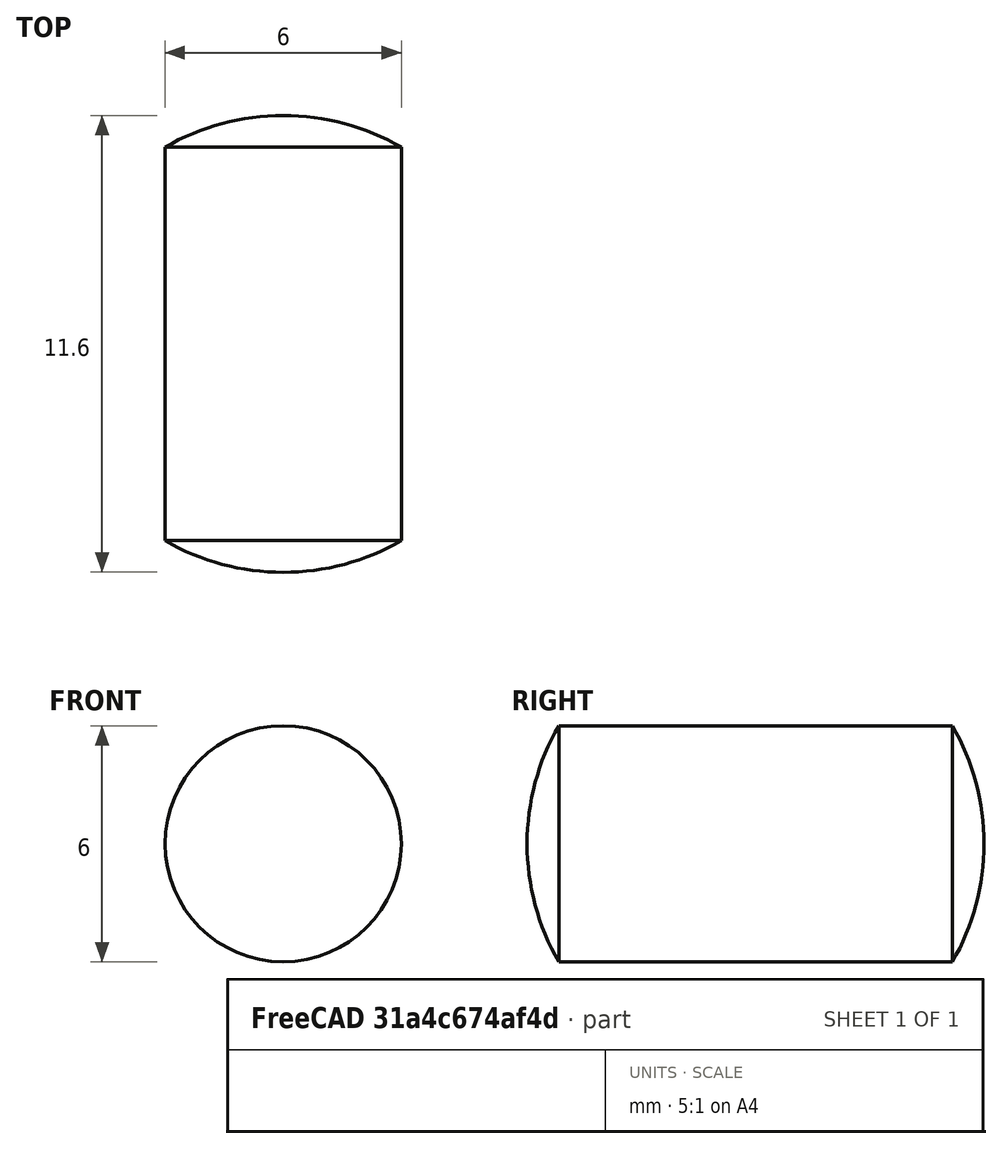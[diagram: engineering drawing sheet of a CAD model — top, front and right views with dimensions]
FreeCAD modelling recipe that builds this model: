
FCSTD DOCUMENT  (FreeCAD 0.15R4470 (Git))
Label: Zyl-Stift_DIN_7-6x10
License: CC-BY 3.0
LicenseURL: http://creativecommons.org/licenses/by/3.0/
objects: Sketcher::SketchObject×1, PartDesign::Revolution×1
note: 3 computed .brp shape members not serialized (recipe doc carries the construction recipe); baked Part::Feature solids carry a one-line shape summary decoded from their .brp

FEATURE [Sketcher::SketchObject] Sketch
  Placement = pos=(0,0,0) rot=(0.57735,0.57735,0.57735;2.0944rad)
  sketch-geometry (4):
    g0: ArcOfCircle CenterX=4.80385 CenterY=0 CenterZ=0 NormalX=0 NormalY=0 NormalZ=1 Radius=6 StartAngle=0 EndAngle=0.523599
    g1: LineSegment StartX=0 StartY=3 StartZ=0 EndX=10 EndY=3 EndZ=0
    g2: LineSegment StartX=-0.803848 StartY=0 StartZ=0 EndX=10.8038 EndY=0 EndZ=0
    g3: ArcOfCircle CenterX=5.19615 CenterY=0 CenterZ=0 NormalX=0 NormalY=0 NormalZ=1 Radius=6 StartAngle=2.61799 EndAngle=3.14159
  constraints (14):
    c: PointOnObject(g2,g-1)
    c: PointOnObject(g1,g-2)
    c: Coincident(g0,g1)
    c: PointOnObject(g0,g-1)
    c: Horizontal(g1)
    c: Coincident(g2,g0)
    c: Horizontal(g2)
    c: Radius(g0) = 6
    c: PointOnObject(g3,g2)
    c: Coincident(g3,g1)
    c: Coincident(g3,g2)
    c: Equal(g3,g0)
    c: DistanceY(g-1,g1) = 3
    c: DistanceX(g1) = 10
FEATURE [PartDesign::Revolution] Revolution  label="Zyl-Stift DIN 7-6x10 #"
  Angle = 360
  Axis = (0,1,0)
  Base = (0,0,0)
  Placement = pos=(0,0,0) rot=(0.57735,0.57735,0.57735;2.0944rad)
  ReferenceAxis = -> Sketch [H_Axis]
  Sketch = -> Sketch
